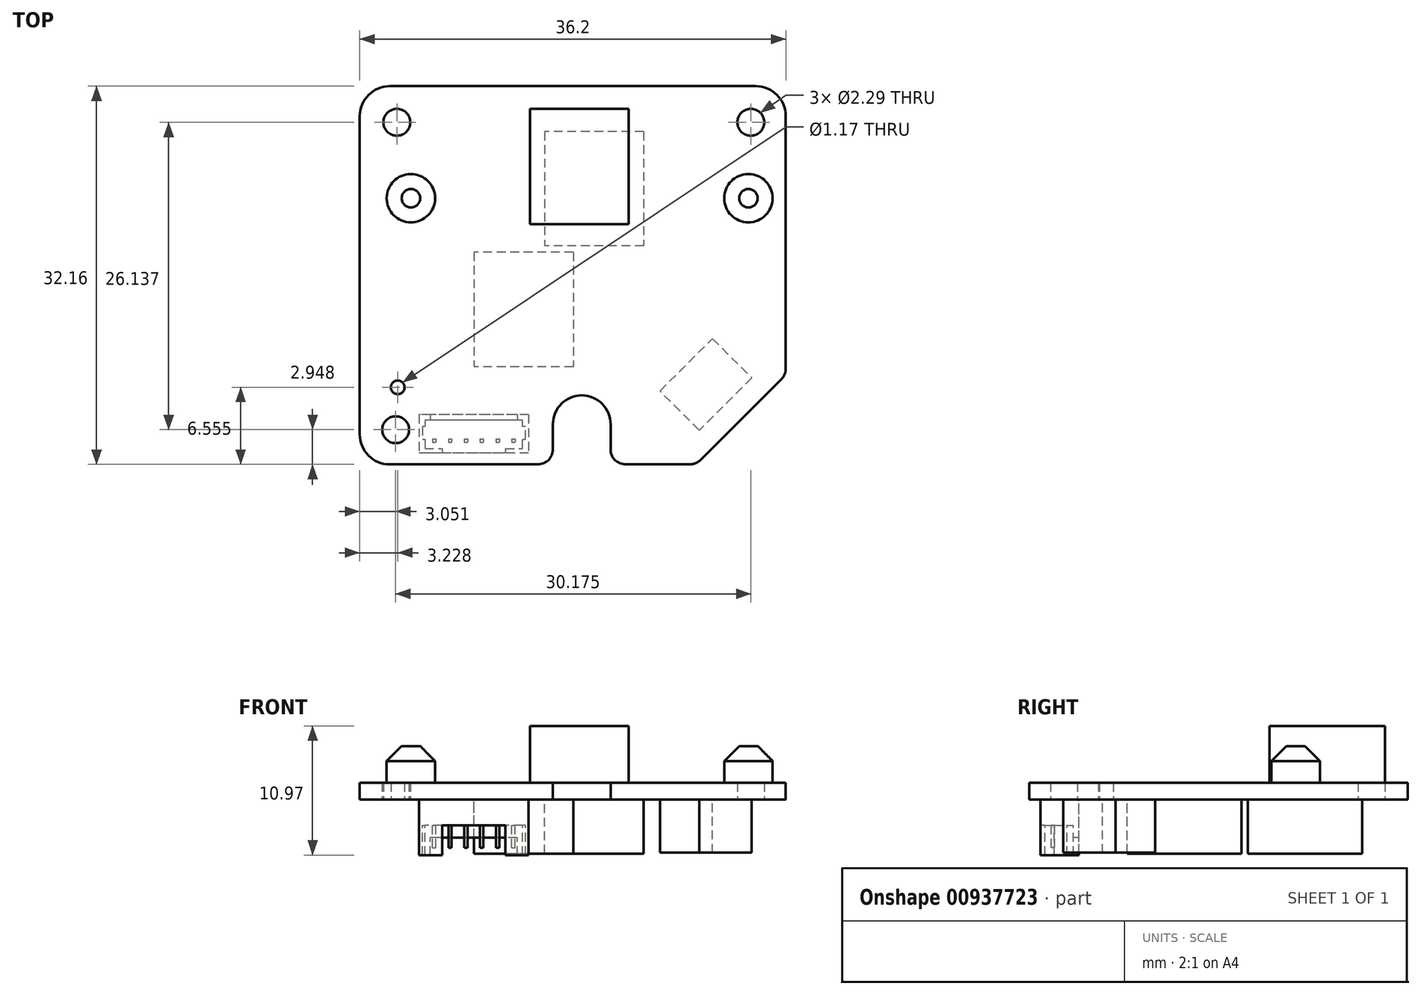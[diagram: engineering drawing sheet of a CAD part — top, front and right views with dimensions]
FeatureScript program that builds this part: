
annotation { "Feature Type Name" : "Feature", "Feature Type Description" : "" }
export const myFeature = defineFeature(function(context is Context, id is Id, definition is map)
    precondition{}
    {
        {
            var Q0;
            Q0=qCreatedBy(makeId("Top.planeOp"),FACE);
            var sketch = newSketch(context, id + "F0", { "sketchPlane" : qUnion([Q0])});
            skLineSegment(sketch, "E0.bottom", {"start": v(-18.1, 16.08) * mm, "end": v(18.1, 16.08) * mm});
            skLineSegment(sketch, "E0.top", {"start": v(-18.1, -16.08) * mm, "end": v(18.1, -16.08) * mm});
            skLineSegment(sketch, "E0.left", {"start": v(-18.1, 16.08) * mm, "end": v(-18.1, -16.08) * mm});
            skLineSegment(sketch, "E0.right", {"start": v(18.1, 16.08) * mm, "end": v(18.1, -16.08) * mm});
            skLineSegment(sketch, "E1", {"start": v(-18.1, 16.08) * mm, "end": v(18.1, -16.08) * mm, "construction": true});
            skLineSegment(sketch, "E2", {"start": v(18.1, 16.08) * mm, "end": v(-18.1, -16.08) * mm, "construction": true});
            skLineSegment(sketch, "E3", {"start": v(18.1, -8.46) * mm, "end": v(10.48, -16.08) * mm});
            skArc(sketch, "E4", {"start": v(18.1, 13.54) * mm, "mid": v(17.35, 15.33) * mm, "end": v(15.56, 16.08) * mm});
            skArc(sketch, "E5", {"start": v(-15.56, 16.08) * mm, "mid": v(-17.35, 15.33) * mm, "end": v(-18.1, 13.54) * mm});
            skArc(sketch, "E6", {"start": v(-18.1, -13.54) * mm, "mid": v(-17.35, -15.33) * mm, "end": v(-15.56, -16.08) * mm});
            skLineSegment(sketch, "E7", {"start": v(3.21, -16.08) * mm, "end": v(3.21, -12.66) * mm});
            skLineSegment(sketch, "E8", {"start": v(-1.69, -16.08) * mm, "end": v(-1.69, -12.66) * mm});
            skArc(sketch, "E9", {"start": v(3.21, -12.66) * mm, "mid": v(0.76, -10.21) * mm, "end": v(-1.69, -12.66) * mm});
            skCircle(sketch, "E10", {"center": v(15.13, 13) * mm, "radius": 1.14 * mm});
            skCircle(sketch, "E11", {"center": v(-14.95, 13) * mm, "radius": 1.14 * mm});
            skCircle(sketch, "E12", {"center": v(-15.05, -13.13) * mm, "radius": 1.14 * mm});
            skCircle(sketch, "E13", {"center": v(-14.87, -9.52) * mm, "radius": 0.58 * mm});
            skArc(sketch, "E14", {"start": v(-2.96, -16.08) * mm, "mid": v(-2.06, -15.7) * mm, "end": v(-1.69, -14.8) * mm});
            skArc(sketch, "E15", {"start": v(3.21, -14.8) * mm, "mid": v(3.59, -15.7) * mm, "end": v(4.48, -16.08) * mm});
            skArc(sketch, "E16", {"start": v(9.95, -16.08) * mm, "mid": v(10.44, -15.98) * mm, "end": v(10.85, -15.7) * mm});
            skArc(sketch, "E17", {"start": v(17.73, -8.83) * mm, "mid": v(18, -8.42) * mm, "end": v(18.1, -7.93) * mm});
            skSolve(sketch);
        }
        {
            var Q0;
            {var subQ4=sQuery(id+"F0.wireOp",EDGE,"E4");Q0=makeQuery(id+"F0.imprint","IMPRINT",FACE,{"disambiguationData":[TD([[makeQuery(id+"F0.imprint","IMPRINT",EDGE,{"derivedFrom":subQ4}),1.0]])]});}
            extrude(context, id + "F1", {"entities" : qUnion([Q0]), "depth" : 1.42 * mm, "offsetDistance" : 25.4 * mm});
        }
        {
            var Q0;
            Q0=makeQuery(id+"F1.opExtrude","CAP_FACE",FACE,{"disambiguationData":[OSD([sQuery(id+"F0.wireOp",EDGE,"E0.bottom"),sQuery(id+"F0.wireOp",EDGE,"E0.top"),sQuery(id+"F0.wireOp",EDGE,"E0.left"),sQuery(id+"F0.wireOp",EDGE,"E0.right"),sQuery(id+"F0.wireOp",EDGE,"E3"),sQuery(id+"F0.wireOp",EDGE,"E4"),sQuery(id+"F0.wireOp",EDGE,"E5"),sQuery(id+"F0.wireOp",EDGE,"E6"),sQuery(id+"F0.wireOp",EDGE,"E7"),sQuery(id+"F0.wireOp",EDGE,"E8"),sQuery(id+"F0.wireOp",EDGE,"E9"),sQuery(id+"F0.wireOp",EDGE,"E10"),sQuery(id+"F0.wireOp",EDGE,"E11"),sQuery(id+"F0.wireOp",EDGE,"E12"),sQuery(id+"F0.wireOp",EDGE,"E13"),sQuery(id+"F0.wireOp",EDGE,"E14"),sQuery(id+"F0.wireOp",EDGE,"E15"),sQuery(id+"F0.wireOp",EDGE,"E16"),sQuery(id+"F0.wireOp",EDGE,"E17")])],"isStart":false});
            var sketch = newSketch(context, id + "F2", { "sketchPlane" : qUnion([Q0])});
            skLineSegment(sketch, "E18.bottom", {"start": v(-3.62, 14.15) * mm, "end": v(4.76, 14.15) * mm});
            skLineSegment(sketch, "E18.top", {"start": v(-3.62, 4.34) * mm, "end": v(4.76, 4.34) * mm});
            skLineSegment(sketch, "E18.left", {"start": v(-3.62, 14.15) * mm, "end": v(-3.62, 4.34) * mm});
            skLineSegment(sketch, "E18.right", {"start": v(4.76, 14.15) * mm, "end": v(4.76, 4.34) * mm});
            skCircle(sketch, "E19", {"center": v(14.92, 6.55) * mm, "radius": 2.06 * mm});
            skCircle(sketch, "E20", {"center": v(-13.75, 6.55) * mm, "radius": 2.06 * mm});
            skLineSegment(sketch, "E21", {"start": v(-13.75, 6.55) * mm, "end": v(14.92, 6.55) * mm, "construction": true});
            skSolve(sketch);
        }
        {
            var Q0;
            Q0=makeQuery(id+"F2.imprint","IMPRINT",FACE,{"disambiguationData":[TD([[makeQuery(id+"F2.imprint","IMPRINT",EDGE,{"derivedFrom":sQuery(id+"F2.wireOp",EDGE,"E18.bottom")}),-1.0]])]});
            extrude(context, id + "F3", {"entities" : qUnion([Q0]), "depth" : 4.83 * mm, "offsetDistance" : 25.4 * mm});
        }
        {
            var Q0;
            Q0=makeQuery(id+"F2.imprint","IMPRINT",FACE,{"disambiguationData":[TD([[makeQuery(id+"F2.imprint","IMPRINT",EDGE,{"derivedFrom":sQuery(id+"F2.wireOp",EDGE,"E20")}),1.0]])]});
            var Q1;
            Q1=makeQuery(id+"F2.imprint","IMPRINT",FACE,{"disambiguationData":[TD([[makeQuery(id+"F2.imprint","IMPRINT",EDGE,{"derivedFrom":sQuery(id+"F2.wireOp",EDGE,"E19")}),1.0]])]});
            extrude(context, id + "F4", {"entities" : qUnion([Q0, Q1]), "operationType" : NewBodyOperationType.ADD, "depth" : 3.12 * mm, "offsetDistance" : 25.4 * mm});
        }
        {
            var Q0;
            Q0=makeQuery(id+"F4.opExtrude","CAP_EDGE",EDGE,{"disambiguationData":[OSD([sQuery(id+"F2.wireOp",EDGE,"E20")])],"isStart":false});
            var Q1;
            Q1=makeQuery(id+"F4.opExtrude","CAP_EDGE",EDGE,{"disambiguationData":[OSD([sQuery(id+"F2.wireOp",EDGE,"E19")])],"isStart":false});
            chamfer(context, id + "F5", {"entities" : qUnion([Q0, Q1]), "width" : 1.27 * mm, "tangentPropagation" : true});
        }
        {
            var Q0;
            Q0=makeQuery(id+"F1.opExtrude","CAP_FACE",FACE,{"disambiguationData":[OSD([sQuery(id+"F0.wireOp",EDGE,"E0.bottom"),sQuery(id+"F0.wireOp",EDGE,"E0.top"),sQuery(id+"F0.wireOp",EDGE,"E0.left"),sQuery(id+"F0.wireOp",EDGE,"E0.right"),sQuery(id+"F0.wireOp",EDGE,"E3"),sQuery(id+"F0.wireOp",EDGE,"E4"),sQuery(id+"F0.wireOp",EDGE,"E5"),sQuery(id+"F0.wireOp",EDGE,"E6"),sQuery(id+"F0.wireOp",EDGE,"E7"),sQuery(id+"F0.wireOp",EDGE,"E8"),sQuery(id+"F0.wireOp",EDGE,"E9"),sQuery(id+"F0.wireOp",EDGE,"E10"),sQuery(id+"F0.wireOp",EDGE,"E11"),sQuery(id+"F0.wireOp",EDGE,"E12"),sQuery(id+"F0.wireOp",EDGE,"E13"),sQuery(id+"F0.wireOp",EDGE,"E14"),sQuery(id+"F0.wireOp",EDGE,"E15"),sQuery(id+"F0.wireOp",EDGE,"E16"),sQuery(id+"F0.wireOp",EDGE,"E17")])],"isStart":true});
            var sketch = newSketch(context, id + "F6", { "sketchPlane" : qUnion([Q0])});
            skLineSegment(sketch, "E22.bottom", {"start": v(6.03, -12.22) * mm, "end": v(-2.4, -12.22) * mm});
            skLineSegment(sketch, "E22.top", {"start": v(6.03, -2.49) * mm, "end": v(-2.4, -2.49) * mm});
            skLineSegment(sketch, "E22.left", {"start": v(6.03, -12.22) * mm, "end": v(6.03, -2.49) * mm});
            skLineSegment(sketch, "E22.right", {"start": v(-2.4, -12.22) * mm, "end": v(-2.4, -2.49) * mm});
            skLineSegment(sketch, "E23.bottom", {"start": v(0.04, -1.96) * mm, "end": v(-8.4, -1.96) * mm});
            skLineSegment(sketch, "E23.top", {"start": v(0.04, 7.77) * mm, "end": v(-8.4, 7.77) * mm});
            skLineSegment(sketch, "E23.left", {"start": v(0.04, -1.96) * mm, "end": v(0.04, 7.77) * mm});
            skLineSegment(sketch, "E23.right", {"start": v(-8.4, -1.96) * mm, "end": v(-8.4, 7.77) * mm});
            skLineSegment(sketch, "E24", {"start": v(15.2, 8.73) * mm, "end": v(10.75, 13.18) * mm});
            skLineSegment(sketch, "E25", {"start": v(10.75, 13.18) * mm, "end": v(7.4, 9.84) * mm});
            skLineSegment(sketch, "E26", {"start": v(7.4, 9.84) * mm, "end": v(11.86, 5.39) * mm});
            skLineSegment(sketch, "E27", {"start": v(11.86, 5.39) * mm, "end": v(15.2, 8.73) * mm});
            skLineSegment(sketch, "E28", {"start": v(12.98, 10.96) * mm, "end": v(14.29, 12.27) * mm, "construction": true});
            skSolve(sketch);
        }
        {
            var Q0;
            Q0=makeQuery(id+"F6.imprint","IMPRINT",FACE,{"disambiguationData":[TD([[makeQuery(id+"F6.imprint","IMPRINT",EDGE,{"derivedFrom":sQuery(id+"F6.wireOp",EDGE,"E22.bottom")}),-1.0]])]});
            var Q1;
            Q1=makeQuery(id+"F6.imprint","IMPRINT",FACE,{"disambiguationData":[TD([[makeQuery(id+"F6.imprint","IMPRINT",EDGE,{"derivedFrom":sQuery(id+"F6.wireOp",EDGE,"E23.bottom")}),-1.0]])]});
            extrude(context, id + "F7", {"entities" : qUnion([Q0, Q1]), "depth" : 4.6 * mm, "offsetDistance" : 25.4 * mm});
        }
        {
            var Q0;
            Q0=makeQuery(id+"F6.imprint","IMPRINT",FACE,{"disambiguationData":[TD([[makeQuery(id+"F6.imprint","IMPRINT",EDGE,{"derivedFrom":sQuery(id+"F6.wireOp",EDGE,"E24")}),1.0]])]});
            extrude(context, id + "F8", {"entities" : qUnion([Q0]), "depth" : 4.52 * mm, "offsetDistance" : 25.4 * mm});
        }
        {
            var Q0;
            Q0=makeQuery(id+"F6.imprint","IMPRINT",FACE,{"disambiguationData":[TD([[makeQuery(id+"F6.imprint","IMPRINT",EDGE,{"derivedFrom":sQuery(id+"F6.wireOp",EDGE,"E22.bottom")}),1.0]])]});
            var sketch = newSketch(context, id + "F9", { "sketchPlane" : qUnion([Q0])});
            skLineSegment(sketch, "E29.bottom", {"start": v(-3.75, 11.86) * mm, "end": v(-13.07, 11.86) * mm});
            skLineSegment(sketch, "E29.top", {"start": v(-3.75, 15.11) * mm, "end": v(-13.07, 15.11) * mm});
            skLineSegment(sketch, "E29.left", {"start": v(-3.75, 11.86) * mm, "end": v(-3.75, 15.11) * mm});
            skLineSegment(sketch, "E29.right", {"start": v(-13.07, 11.86) * mm, "end": v(-13.07, 15.11) * mm});
            skLineSegment(sketch, "E30", {"start": v(-4.25, 12.32) * mm, "end": v(-12.56, 12.32) * mm});
            skLineSegment(sketch, "E31", {"start": v(-12.56, 12.32) * mm, "end": v(-12.56, 12.88) * mm});
            skLineSegment(sketch, "E32", {"start": v(-12.56, 12.88) * mm, "end": v(-12.79, 12.88) * mm});
            skLineSegment(sketch, "E33", {"start": v(-12.79, 12.88) * mm, "end": v(-12.79, 13.94) * mm});
            skLineSegment(sketch, "E34", {"start": v(-12.79, 13.94) * mm, "end": v(-12.56, 13.94) * mm});
            skLineSegment(sketch, "E35", {"start": v(-12.56, 13.94) * mm, "end": v(-12.56, 14.73) * mm});
            skLineSegment(sketch, "E36", {"start": v(-12.56, 14.73) * mm, "end": v(-4.25, 14.73) * mm});
            skLineSegment(sketch, "E37", {"start": v(-4.25, 14.73) * mm, "end": v(-4.25, 13.94) * mm});
            skLineSegment(sketch, "E38", {"start": v(-4.25, 13.94) * mm, "end": v(-4.03, 13.94) * mm});
            skLineSegment(sketch, "E39", {"start": v(-4.03, 13.94) * mm, "end": v(-4.03, 12.88) * mm});
            skLineSegment(sketch, "E40", {"start": v(-4.03, 12.88) * mm, "end": v(-4.25, 12.88) * mm});
            skLineSegment(sketch, "E41", {"start": v(-4.25, 12.88) * mm, "end": v(-4.25, 12.32) * mm});
            skLineSegment(sketch, "E42", {"start": v(-12.1, 11.86) * mm, "end": v(-12.1, 12.32) * mm});
            skLineSegment(sketch, "E43", {"start": v(-4.71, 11.86) * mm, "end": v(-4.71, 12.32) * mm});
            skLineSegment(sketch, "E44", {"start": v(-11.09, 14.73) * mm, "end": v(-11.09, 15.11) * mm});
            skLineSegment(sketch, "E45", {"start": v(-5.73, 14.73) * mm, "end": v(-5.73, 15.11) * mm});
            skSolve(sketch);
        }
        {
            var Q0;
            {var subQ8=sQuery(id+"F9.wireOp",EDGE,"E31");Q0=makeQuery(id+"F9.imprint","IMPRINT",FACE,{"disambiguationData":[TD([[makeQuery(id+"F9.imprint","IMPRINT",EDGE,{"derivedFrom":subQ8}),-1.0]])]});}
            var Q1;
            {var subQ0=sQuery(id+"F9.wireOp",EDGE,"E44");Q1=makeQuery(id+"F9.imprint","IMPRINT",FACE,{"disambiguationData":[TD([[makeQuery(id+"F9.imprint","IMPRINT",EDGE,{"derivedFrom":subQ0}),-1.0]])]});}
            extrude(context, id + "F10", {"entities" : qUnion([Q0, Q1]), "depth" : 2.18 * mm, "offsetDistance" : 25.4 * mm});
        }
        {
            var Q0;
            {var subQ1=sQuery(id+"F9.wireOp",EDGE,"E29.left");Q0=makeQuery(id+"F9.imprint","IMPRINT",FACE,{"disambiguationData":[TD([[makeQuery(id+"F9.imprint","IMPRINT",EDGE,{"derivedFrom":subQ1}),1.0]])]});}
            var Q1;
            {var subQ2=sQuery(id+"F9.wireOp",EDGE,"E29.right");Q1=makeQuery(id+"F9.imprint","IMPRINT",FACE,{"disambiguationData":[TD([[makeQuery(id+"F9.imprint","IMPRINT",EDGE,{"derivedFrom":subQ2}),-1.0]])]});}
            extrude(context, id + "F11", {"entities" : qUnion([Q0, Q1]), "operationType" : NewBodyOperationType.ADD, "depth" : 4.72 * mm, "offsetDistance" : 25.4 * mm});
        }
        {
            var Q0;
            {var subQ0=sQuery(id+"F9.wireOp",EDGE,"E42");Q0=makeQuery(id+"F9.imprint","IMPRINT",FACE,{"disambiguationData":[TD([[makeQuery(id+"F9.imprint","IMPRINT",EDGE,{"derivedFrom":subQ0}),-1.0]])]});}
            extrude(context, id + "F12", {"entities" : qUnion([Q0]), "operationType" : NewBodyOperationType.ADD, "depth" : 3.23 * mm, "offsetDistance" : 25.4 * mm});
        }
        {
            var Q0;
            Q0=makeQuery(id+"F10.opExtrude","CAP_FACE",FACE,{"disambiguationData":[OSD([sQuery(id+"F9.wireOp",EDGE,"E29.top"),sQuery(id+"F9.wireOp",EDGE,"E30"),sQuery(id+"F9.wireOp",EDGE,"E31"),sQuery(id+"F9.wireOp",EDGE,"E32"),sQuery(id+"F9.wireOp",EDGE,"E33"),sQuery(id+"F9.wireOp",EDGE,"E34"),sQuery(id+"F9.wireOp",EDGE,"E35"),sQuery(id+"F9.wireOp",EDGE,"E36"),sQuery(id+"F9.wireOp",EDGE,"E37"),sQuery(id+"F9.wireOp",EDGE,"E38"),sQuery(id+"F9.wireOp",EDGE,"E39"),sQuery(id+"F9.wireOp",EDGE,"E40"),sQuery(id+"F9.wireOp",EDGE,"E41"),sQuery(id+"F9.wireOp",EDGE,"E44"),sQuery(id+"F9.wireOp",EDGE,"E45")])],"isStart":false});
            var sketch = newSketch(context, id + "F13", { "sketchPlane" : qUnion([Q0])});
            skLineSegment(sketch, "E46.bottom", {"start": v(-11.91, 13.92) * mm, "end": v(-11.63, 13.92) * mm});
            skLineSegment(sketch, "E46.top", {"start": v(-11.91, 14.2) * mm, "end": v(-11.63, 14.2) * mm});
            skLineSegment(sketch, "E46.left", {"start": v(-11.91, 13.92) * mm, "end": v(-11.91, 14.2) * mm});
            skLineSegment(sketch, "E46.right", {"start": v(-11.63, 13.92) * mm, "end": v(-11.63, 14.2) * mm});
            skLineSegment(sketch, "E47.bottom", {"start": v(-10.57, 13.92) * mm, "end": v(-10.29, 13.92) * mm});
            skLineSegment(sketch, "E47.top", {"start": v(-10.57, 14.2) * mm, "end": v(-10.29, 14.2) * mm});
            skLineSegment(sketch, "E47.left", {"start": v(-10.57, 13.92) * mm, "end": v(-10.57, 14.2) * mm});
            skLineSegment(sketch, "E47.right", {"start": v(-10.29, 13.92) * mm, "end": v(-10.29, 14.2) * mm});
            skLineSegment(sketch, "E48.bottom", {"start": v(-9.22, 13.92) * mm, "end": v(-8.94, 13.92) * mm});
            skLineSegment(sketch, "E48.top", {"start": v(-9.22, 14.2) * mm, "end": v(-8.94, 14.2) * mm});
            skLineSegment(sketch, "E48.left", {"start": v(-9.22, 13.92) * mm, "end": v(-9.22, 14.2) * mm});
            skLineSegment(sketch, "E48.right", {"start": v(-8.94, 13.92) * mm, "end": v(-8.94, 14.2) * mm});
            skLineSegment(sketch, "E49.bottom", {"start": v(-7.87, 13.92) * mm, "end": v(-7.6, 13.92) * mm});
            skLineSegment(sketch, "E49.top", {"start": v(-7.87, 14.2) * mm, "end": v(-7.6, 14.2) * mm});
            skLineSegment(sketch, "E49.left", {"start": v(-7.87, 13.92) * mm, "end": v(-7.87, 14.2) * mm});
            skLineSegment(sketch, "E49.right", {"start": v(-7.6, 13.92) * mm, "end": v(-7.6, 14.2) * mm});
            skLineSegment(sketch, "E50.bottom", {"start": v(-6.53, 13.92) * mm, "end": v(-6.25, 13.92) * mm});
            skLineSegment(sketch, "E50.top", {"start": v(-6.53, 14.2) * mm, "end": v(-6.25, 14.2) * mm});
            skLineSegment(sketch, "E50.left", {"start": v(-6.53, 13.92) * mm, "end": v(-6.53, 14.2) * mm});
            skLineSegment(sketch, "E50.right", {"start": v(-6.25, 13.92) * mm, "end": v(-6.25, 14.2) * mm});
            skLineSegment(sketch, "E51.bottom", {"start": v(-5.18, 13.92) * mm, "end": v(-4.9, 13.92) * mm});
            skLineSegment(sketch, "E51.top", {"start": v(-5.18, 14.2) * mm, "end": v(-4.9, 14.2) * mm});
            skLineSegment(sketch, "E51.left", {"start": v(-5.18, 13.92) * mm, "end": v(-5.18, 14.2) * mm});
            skLineSegment(sketch, "E51.right", {"start": v(-4.9, 13.92) * mm, "end": v(-4.9, 14.2) * mm});
            skLineSegment(sketch, "E52", {"start": v(-4.25, 14.2) * mm, "end": v(-4.9, 14.2) * mm, "construction": true});
            skLineSegment(sketch, "E53", {"start": v(-5.18, 14.2) * mm, "end": v(-6.25, 14.2) * mm, "construction": true});
            skLineSegment(sketch, "E54", {"start": v(-6.53, 14.2) * mm, "end": v(-7.6, 14.2) * mm, "construction": true});
            skLineSegment(sketch, "E55", {"start": v(-7.87, 14.2) * mm, "end": v(-8.94, 14.2) * mm, "construction": true});
            skLineSegment(sketch, "E56", {"start": v(-9.22, 14.2) * mm, "end": v(-10.29, 14.2) * mm, "construction": true});
            skLineSegment(sketch, "E57", {"start": v(-10.57, 14.2) * mm, "end": v(-11.63, 14.2) * mm, "construction": true});
            skLineSegment(sketch, "E58", {"start": v(-11.91, 14.2) * mm, "end": v(-12.56, 14.2) * mm, "construction": true});
            skSolve(sketch);
        }
        {
            var Q0;
            Q0=makeQuery(id+"F13.imprint","IMPRINT",FACE,{"disambiguationData":[TD([[makeQuery(id+"F13.imprint","IMPRINT",EDGE,{"derivedFrom":sQuery(id+"F13.wireOp",EDGE,"E46.bottom")}),1.0]])]});
            var Q1;
            Q1=makeQuery(id+"F13.imprint","IMPRINT",FACE,{"disambiguationData":[TD([[makeQuery(id+"F13.imprint","IMPRINT",EDGE,{"derivedFrom":sQuery(id+"F13.wireOp",EDGE,"E47.bottom")}),1.0]])]});
            var Q2;
            Q2=makeQuery(id+"F13.imprint","IMPRINT",FACE,{"disambiguationData":[TD([[makeQuery(id+"F13.imprint","IMPRINT",EDGE,{"derivedFrom":sQuery(id+"F13.wireOp",EDGE,"E48.bottom")}),1.0]])]});
            var Q3;
            Q3=makeQuery(id+"F13.imprint","IMPRINT",FACE,{"disambiguationData":[TD([[makeQuery(id+"F13.imprint","IMPRINT",EDGE,{"derivedFrom":sQuery(id+"F13.wireOp",EDGE,"E51.bottom")}),1.0]])]});
            var Q4;
            Q4=makeQuery(id+"F13.imprint","IMPRINT",FACE,{"disambiguationData":[TD([[makeQuery(id+"F13.imprint","IMPRINT",EDGE,{"derivedFrom":sQuery(id+"F13.wireOp",EDGE,"E50.bottom")}),1.0]])]});
            var Q5;
            Q5=makeQuery(id+"F13.imprint","IMPRINT",FACE,{"disambiguationData":[TD([[makeQuery(id+"F13.imprint","IMPRINT",EDGE,{"derivedFrom":sQuery(id+"F13.wireOp",EDGE,"E49.bottom")}),1.0]])]});
            extrude(context, id + "F14", {"entities" : qUnion([Q0, Q1, Q2, Q3, Q4, Q5]), "operationType" : NewBodyOperationType.ADD, "depth" : 1.9 * mm, "offsetDistance" : 25.4 * mm});
        }
    });
